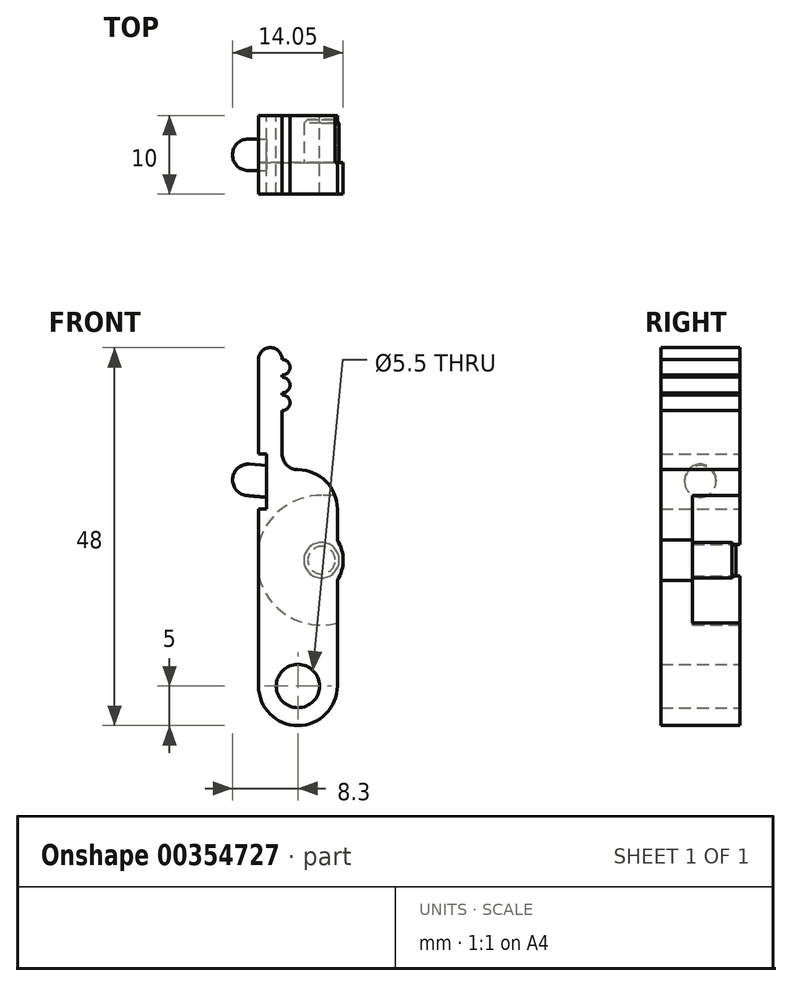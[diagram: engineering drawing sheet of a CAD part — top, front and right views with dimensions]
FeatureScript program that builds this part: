
annotation { "Feature Type Name" : "Feature", "Feature Type Description" : "" }
export const myFeature = defineFeature(function(context is Context, id is Id, definition is map)
    precondition{}
    {
        {
            var Q0;
            Q0=qCreatedBy(makeId("Front.planeOp"),FACE);
            var sketch = newSketch(context, id + "F0", { "sketchPlane" : qUnion([Q0])});
            skLineSegment(sketch, "E0", {"start": v(-5, 41.5) * mm, "end": v(-5, 29.5) * mm});
            skLineSegment(sketch, "E1", {"start": v(-5, 29.5) * mm, "end": v(-4, 29.5) * mm});
            skLineSegment(sketch, "E2", {"start": v(-4, 29.5) * mm, "end": v(-4, 22.5) * mm});
            skLineSegment(sketch, "E3", {"start": v(-4, 22.5) * mm, "end": v(-5, 22.5) * mm});
            skLineSegment(sketch, "E4", {"start": v(-5, 22.5) * mm, "end": v(-5, 0) * mm});
            skLineSegment(sketch, "E5", {"start": v(5, 0) * mm, "end": v(5, 13.44) * mm});
            skLineSegment(sketch, "E6", {"start": v(5, 18.56) * mm, "end": v(5, 27.5) * mm});
            skArc(sketch, "E7", {"start": v(5, 0) * mm, "mid": v(0, -5) * mm, "end": v(-5, 0) * mm});
            skCircle(sketch, "E8", {"center": v(0, 0) * mm, "radius": 2.75 * mm});
            skPoint(sketch, "E9", {"position": v(-4, 26) * mm});
            skArc(sketch, "E10", {"start": v(-5, 41.5) * mm, "mid": v(-3.5, 43) * mm, "end": v(-2, 41.5) * mm});
            skLineSegment(sketch, "E11", {"start": v(-2, 41.5) * mm, "end": v(-2, 29.5) * mm});
            skLineSegment(sketch, "E12", {"start": v(0, 27.5) * mm, "end": v(5, 27.5) * mm});
            skArc(sketch, "E13", {"start": v(-2, 41.5) * mm, "mid": v(-1, 40.5) * mm, "end": v(-2, 39.5) * mm});
            skArc(sketch, "E14.1.0.0", {"start": v(-2, 39.25) * mm, "mid": v(-1, 38.25) * mm, "end": v(-2, 37.25) * mm});
            skArc(sketch, "E14.2.0.0", {"start": v(-2, 37) * mm, "mid": v(-1, 36) * mm, "end": v(-2, 35) * mm});
            skPoint(sketch, "E15.visualSharp", {"position": v(-2, 27.5) * mm});
            skArc(sketch, "E15.filletArc", {"start": v(-2, 29.5) * mm, "mid": v(-1.41, 28.09) * mm, "end": v(0, 27.5) * mm});
            skCircle(sketch, "E16", {"center": v(1, 16) * mm, "radius": 2.75 * mm, "construction": true});
            skArc(sketch, "E17.0", {"start": v(5, 13.44) * mm, "mid": v(5.75, 16) * mm, "end": v(5, 18.56) * mm});
            skCircle(sketch, "E18", {"center": v(1, 16) * mm, "radius": 8 * mm, "construction": true});
            skSolve(sketch);
        }
        {
            var Q0;
            Q0=qSketchRegion(id+"F0",true);
            extrude(context, id + "F1", {"entities" : qUnion([Q0]), "endBound" : BoundingType.SYMMETRIC, "depth" : 10 * mm});
        }
        {
            var Q0;
            Q0=qCreatedBy(makeId("Front.planeOp"),FACE);
            var sketch = newSketch(context, id + "F2", { "sketchPlane" : qUnion([Q0])});
            skLineSegment(sketch, "E19.0", {"start": v(-4, 29.5) * mm, "end": v(-4, 22.5) * mm, "construction": true});
            skPoint(sketch, "E20", {"position": v(-4, 26) * mm});
            skLineSegment(sketch, "E21", {"start": v(-3.31, 25.94) * mm, "end": v(-4.6, 26.05) * mm, "construction": true});
            skLineSegment(sketch, "E22", {"start": v(-3.14, 27.93) * mm, "end": v(-6.13, 28.2) * mm});
            skArc(sketch, "E23", {"start": v(-6.13, 28.2) * mm, "mid": v(-7.59, 27.73) * mm, "end": v(-8.3, 26.38) * mm});
            skLineSegment(sketch, "E24", {"start": v(-3.14, 27.93) * mm, "end": v(-3.31, 25.94) * mm});
            skLineSegment(sketch, "E25", {"start": v(-8.3, 26.38) * mm, "end": v(-3.31, 25.94) * mm});
            skLineSegment(sketch, "E26.0", {"start": v(-5, 29.5) * mm, "end": v(-4, 29.5) * mm, "construction": true});
            skLineSegment(sketch, "E26.2", {"start": v(-4, 22.5) * mm, "end": v(-5, 22.5) * mm, "construction": true});
            skLineSegment(sketch, "E27", {"start": v(3.32, 26) * mm, "end": v(-13.3, 26) * mm, "construction": true});
            skSolve(sketch);
        }
        {
            var Q0;
            Q0=qSketchRegion(id+"F2",true);
            var Q1;
            Q1=sQuery(id+"F2.wireOp",EDGE,"E21");
            revolve(context, id + "F3", {"operationType" : NewBodyOperationType.ADD, "entities" : qUnion([Q0]), "axis" : qUnion([Q1]), "revolveType" : RevolveType.FULL});
        }
        {
            var Q0;
            Q0=qCreatedBy(makeId("Right.planeOp"),FACE);
            cPlane(context, id + "F4", {"entities" : qUnion([Q0]), "cplaneType" : CPlaneType.OFFSET, "offset" : 3 * mm, "width" : 150 * mm, "height" : 150 * mm});
        }
        {
            var Q0;
            Q0=qCreatedBy(id+"F4.planeOp",FACE);
            var sketch = newSketch(context, id + "F5", { "sketchPlane" : qUnion([Q0])});
            skLineSegment(sketch, "E28.bottom", {"start": v(5, 24.25) * mm, "end": v(-1, 24.25) * mm});
            skLineSegment(sketch, "E28.top", {"start": v(5, 7.75) * mm, "end": v(-1, 7.75) * mm, "construction": true});
            skLineSegment(sketch, "E28.left", {"start": v(5, 24.25) * mm, "end": v(5, 16) * mm});
            skLineSegment(sketch, "E28.right", {"start": v(-1, 24.25) * mm, "end": v(-1, 16) * mm});
            skPoint(sketch, "E28.middle", {"position": v(2, 16) * mm});
            skLineSegment(sketch, "E29.0", {"start": v(-5, 13.44) * mm, "end": v(5, 13.44) * mm, "construction": true});
            skLineSegment(sketch, "E29.1", {"start": v(-5, 18.56) * mm, "end": v(5, 18.56) * mm, "construction": true});
            skLineSegment(sketch, "E30", {"start": v(0, 18.56) * mm, "end": v(0, 13.44) * mm, "construction": true});
            skPoint(sketch, "E31", {"position": v(0, 16) * mm});
            skLineSegment(sketch, "E32", {"start": v(-5.76, 16) * mm, "end": v(5.86, 16) * mm, "construction": true});
            skLineSegment(sketch, "E33", {"start": v(-1, 16) * mm, "end": v(-1, 7.75) * mm, "construction": true});
            skLineSegment(sketch, "E34", {"start": v(5, 16) * mm, "end": v(5, 7.75) * mm, "construction": true});
            skLineSegment(sketch, "E35", {"start": v(-1, 16) * mm, "end": v(5, 16) * mm});
            skLineSegment(sketch, "E36", {"start": v(2.35, 31.23) * mm, "end": v(2.35, 5.02) * mm, "construction": true});
            skSolve(sketch);
        }
        {
            var Q0;
            Q0=qSketchRegion(id+"F5",true);
            var Q1;
            Q1=sQuery(id+"F5.wireOp",EDGE,"E32");
            revolve(context, id + "F6", {"operationType" : NewBodyOperationType.REMOVE, "entities" : qUnion([Q0]), "axis" : qUnion([Q1]), "revolveType" : RevolveType.FULL, "oppositeDirection" : true});
        }
        {
            var Q0;
            Q0=qSketchRegion(id+"F5",true);
            extrude(context, id + "F7", {"entities" : qUnion([Q0]), "operationType" : NewBodyOperationType.REMOVE, "endBound" : BoundingType.THROUGH_ALL, "depth" : 25 * mm});
        }
        {
            var Q0;
            Q0=makeQuery(id+"F1.opExtrude","SWEPT_EDGE",EDGE,{"disambiguationData":[OSD([sQuery(id+"F0.wireOp",EDGE,"E6"),sQuery(id+"F0.wireOp",EDGE,"E12")])]});
            fillet(context, id + "F8", {"entities" : qUnion([Q0]), "radius" : 5 * mm, "tangentPropagation" : true, "allowEdgeOverflow" : false});
        }
        {
            var Q0;
            {var subQ0=sQuery(id+"F5.wireOp",EDGE,"E28.right");Q0=makeQuery(id+"F7.boolean.opBoolean","MERGE",FACE,{"derivedFrom":[makeQuery(id+"F6.boolean.opBoolean","COPY",FACE,{"derivedFrom":makeQuery(id+"F6.opRevolve","SWEPT_FACE",FACE,{"disambiguationData":[OSD([subQ0])]})}),makeQuery(id+"F7.opExtrude","SWEPT_FACE",FACE,{"disambiguationData":[OSD([subQ0])]})]});}
            var sketch = newSketch(context, id + "F9", { "sketchPlane" : qUnion([Q0])});
            skCircle(sketch, "E37", {"center": v(-3, 16) * mm, "radius": 2.25 * mm});
            skSolve(sketch);
        }
        {
            var Q0;
            Q0=qSketchRegion(id+"F9",true);
            extrude(context, id + "F10", {"entities" : qUnion([Q0]), "operationType" : NewBodyOperationType.ADD, "depth" : 5.5 * mm});
        }
        {
            var Q0;
            Q0=makeQuery(id+"F10.opExtrude","CAP_EDGE",EDGE,{"disambiguationData":[OSD([sQuery(id+"F9.wireOp",EDGE,"E37")])],"isStart":false});
            chamfer(context, id + "F11", {"entities" : qUnion([Q0]), "width" : .5 * mm, "tangentPropagation" : true});
        }
    });
